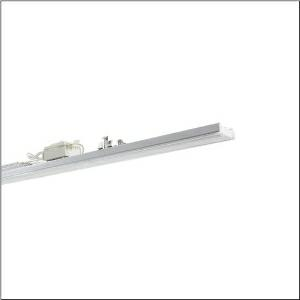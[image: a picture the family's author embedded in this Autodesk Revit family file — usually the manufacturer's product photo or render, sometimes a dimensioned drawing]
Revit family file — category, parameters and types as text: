
# Revit family: licross_r__21_recessed_mo_52te12dv4fxg3s4_28ef
name_source: partatom
category: Lighting Fixtures
units: mm (PartAtom-declared; Revit-internal decimal feet)

## family parameters
Cut with Voids When Loaded = No
Host = Face
Light Source = No
Part Type = Normal
Room Calculation Point = No
Round Connector Dimension = Use Diameter
Shared = No

## types (1)
- --- (1 x LED, 950 lm, 5.5 W, 4000K)
    Apparent Load = 6 VA
    CIE Flux Codes = 72 92 99 100 100
    Color Rendering = 80
    Color Temperature = 4000K
    Default Elevation = 1800 mm
    Description = Licross® 21 Recessed MO, luminaire insert, of sheet steel, galvanised, coil coated, white, length: 2.250mm, width: 66mm, height: 67mm, LED rated luminous flux: 15.420lm, light colour: 840, control gear: DALI 2, with plug, 6-pole, with phase selection, for trunking rail, 9 or 11-core, mains connection: 220..240V, AC, 50/60Hz, rated input power: 89W, for trunking rail, 9-/11-core, internal wiring halogen-free, for emergency light function, converter,control gear: single battery element, battery: LiFePO4, 9Ah, primary optical cover: cover, of PMMA, light emission: direct distribution, primary light characteristic: symmetric, protection rating (complete): IP54, insulation class (complete): insulation class I (protective earthing), certification: CE, UKCA, protection symbol: D if used in an environment with non-conductive dust loads with corresponding accessories, impact resistance: IK06, permissible ambient temperature for indoor applications: +5..+35°C, standard: EN 60598-2-22, LABS conformity tested according to VDMA 24364:2018-05, reducing of maximum allowable ambient temperature of 5°C with ceiling mounting, corresponds to IFS (International Featured Standards) requirements for safety and quality in the food industry, packaging unit: 1 piece
    Height = 58 mm
    Lamp = 1 x LED
    Lamp Light Flux = 950 lm
    Lamp Power = 5.5 W
    Lamp count = 1
    Length = 2250 mm
    Luminous efficacy = 173 lm/W
    Manufacturer = Siteco
    ModVariant = No
    Model = 52TE12DV4FXG3S4
    Mounting Place = Ceiling
    Mounting Type = Pendant
    Number of Poles = 1
    OnlyDefault = Yes
    Power Factor = 1
    Product Name = Licross® 21 Recessed MO
    Product group = luminaire insert | ceiling pendant
    ProductGroupID = 902
    Protection Class = Protection class I
    Protection Degree = IP 54
    RLX_Detail_Level = 1
    RLX_Emergency_Light_Flux = 0 lm
    RLX_Emergency_Type = 0
    RLX_Emergency_Type_DB = No
    RlxData = <blob elided: 29757 chars, md5=6f787126>
    Socket = socket
    Standby Power = 0 W
    System Light Flux = 950 lm
    System Power = 6 W
    Type Comments = : emergency light operation: 3 h
    Type Image = l_1296930.jpg
    URL = http://relux.com
    VarID = @adj_131539
    Voltage = 0 V
    Weight = 0.00 kg
    Width = 66 mm

## geometry (parser evidence)
native form markers: Blend x4, Sweep x9
no freeform markers — native parametric forms only
